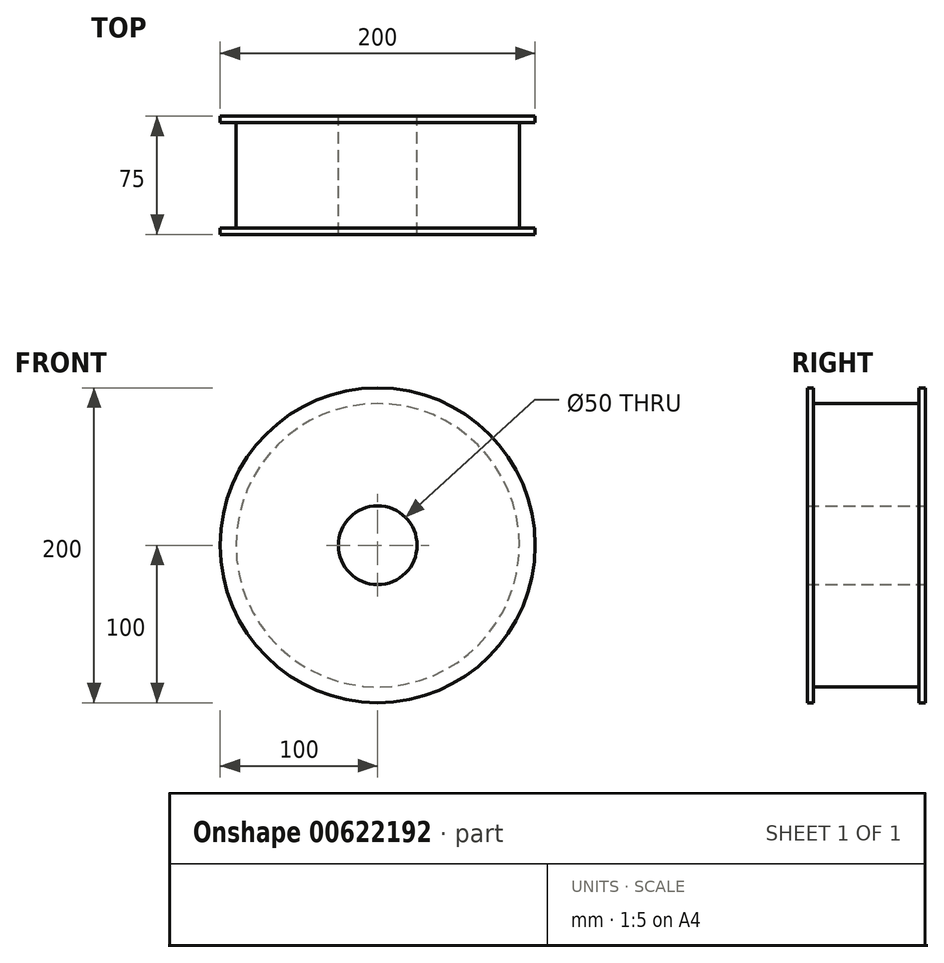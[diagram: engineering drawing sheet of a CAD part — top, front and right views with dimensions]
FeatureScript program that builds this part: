
annotation { "Feature Type Name" : "Feature", "Feature Type Description" : "" }
export const myFeature = defineFeature(function(context is Context, id is Id, definition is map)
    precondition{}
    {
        {
            var Q0;
            Q0=qCreatedBy(makeId("Front.planeOp"),FACE);
            var sketch = newSketch(context, id + "F0", { "sketchPlane" : qUnion([Q0])});
            skCircle(sketch, "E0", {"center": v(0, 0) * mm, "radius": 100 * mm});
            skCircle(sketch, "E1", {"center": v(0, 0) * mm, "radius": 25 * mm});
            skSolve(sketch);
        }
        {
            var Q0;
            Q0=makeQuery(id+"F0.imprint","IMPRINT",FACE,{"disambiguationData":[TD([[makeQuery(id+"F0.imprint","IMPRINT",EDGE,{"derivedFrom":sQuery(id+"F0.wireOp",EDGE,"E0")}),1.0]])]});
            extrude(context, id + "F1", {"entities" : qUnion([Q0]), "depth" : 75 * mm, "offsetDistance" : 25 * mm});
        }
        {
            var Q0;
            Q0=qCreatedBy(makeId("Right.planeOp"),FACE);
            var sketch = newSketch(context, id + "F2", { "sketchPlane" : qUnion([Q0])});
            skLineSegment(sketch, "E2", {"start": v(0, 0) * mm, "end": v(0, 100) * mm, "construction": true});
            skLineSegment(sketch, "E3", {"start": v(0, 100) * mm, "end": v(-4, 100) * mm, "construction": true});
            skLineSegment(sketch, "E4", {"start": v(-4, 100) * mm, "end": v(-4, 90) * mm});
            skLineSegment(sketch, "E5", {"start": v(-4, 90) * mm, "end": v(-71, 90) * mm});
            skLineSegment(sketch, "E6", {"start": v(-71, 90) * mm, "end": v(-71, 100) * mm});
            skLineSegment(sketch, "E7", {"start": v(-71, 100) * mm, "end": v(-75, 100) * mm, "construction": true});
            skLineSegment(sketch, "E8", {"start": v(-75, 100) * mm, "end": v(-75, 0) * mm, "construction": true});
            skLineSegment(sketch, "E9", {"start": v(-75, 0) * mm, "end": v(0, 0) * mm, "construction": true});
            skLineSegment(sketch, "E10", {"start": v(-71, 100) * mm, "end": v(-4, 100) * mm});
            skSolve(sketch);
        }
        {
            var Q0;
            Q0=makeQuery(id+"F2.imprint","IMPRINT",FACE,{"disambiguationData":[TD([[makeQuery(id+"F2.imprint","IMPRINT",EDGE,{"derivedFrom":sQuery(id+"F2.wireOp",EDGE,"E4")}),-1.0]])]});
            var Q1;
            Q1=sQuery(id+"F2.wireOp",EDGE,"E9");
            revolve(context, id + "F3", {"operationType" : NewBodyOperationType.REMOVE, "entities" : qUnion([Q0]), "axis" : qUnion([Q1]), "revolveType" : RevolveType.FULL, "oppositeDirection" : true});
        }
    });
